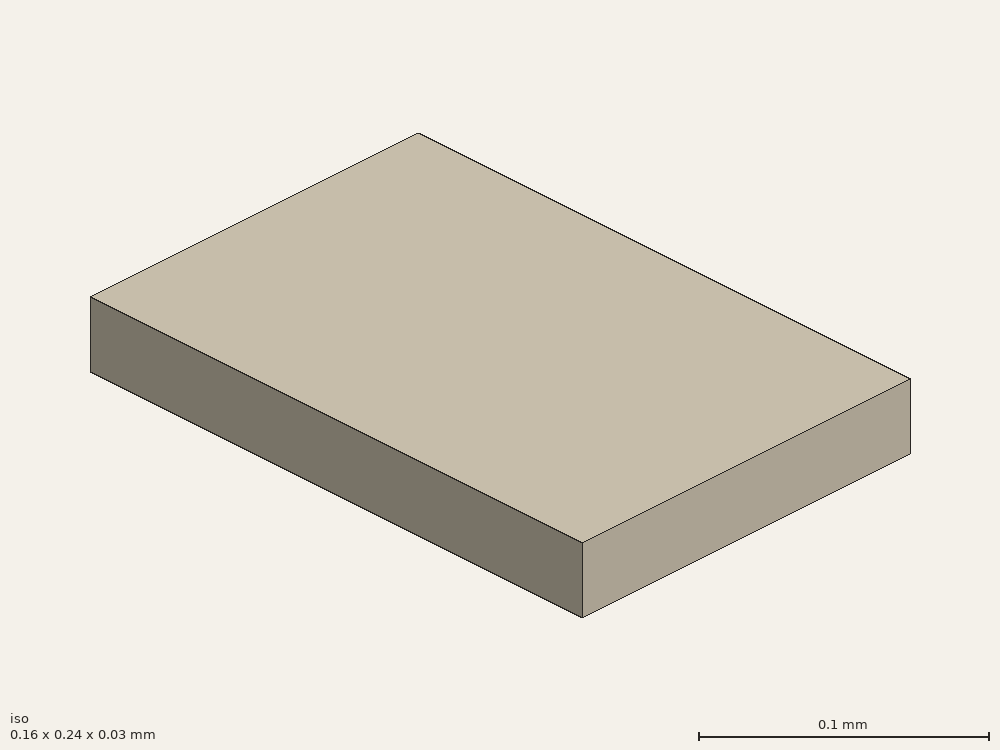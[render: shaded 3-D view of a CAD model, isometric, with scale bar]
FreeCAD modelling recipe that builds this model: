
FCSTD DOCUMENT  (FreeCAD 0.15R4671 (Git))
Label: quadrangle2
License: All rights reserved
LicenseURL: http://en.wikipedia.org/wiki/All_rights_reserved
objects: Sketcher::SketchObject×1, PartDesign::Pad×1
note: 3 computed .brp shape members not serialized (recipe doc carries the construction recipe); baked Part::Feature solids carry a one-line shape summary decoded from their .brp

FEATURE [Sketcher::SketchObject] Sketch
  sketch-geometry (4):
    g0: LineSegment StartX=0.08 StartY=0.12 StartZ=0 EndX=-0.08 EndY=0.12 EndZ=0
    g1: LineSegment StartX=-0.08 StartY=0.12 StartZ=0 EndX=-0.08 EndY=-0.12 EndZ=0
    g2: LineSegment StartX=-0.08 StartY=-0.12 StartZ=0 EndX=0.08 EndY=-0.12 EndZ=0
    g3: LineSegment StartX=0.08 StartY=-0.12 StartZ=0 EndX=0.08 EndY=0.12 EndZ=0
  constraints (13):
    c: Coincident(g0,g1)
    c: Coincident(g1,g2)
    c: Coincident(g2,g3)
    c: Coincident(g3,g0)
    c: Horizontal(g0)
    c: Horizontal(g2)
    c: Vertical(g1)
    c: Vertical(g3)
    c: Symmetric(g0,g2,g-1)
    c: Equal(g0,g2)
    c: Equal(g3,g1)
    c: DistanceY(g0,g1) = -0.24
    c: DistanceX(g0,g0) = 0.16
FEATURE [PartDesign::Pad] Pad
  Length = 0.03
  Length2 = 100
  Midplane = true
  Sketch = -> Sketch
  Type = 0
